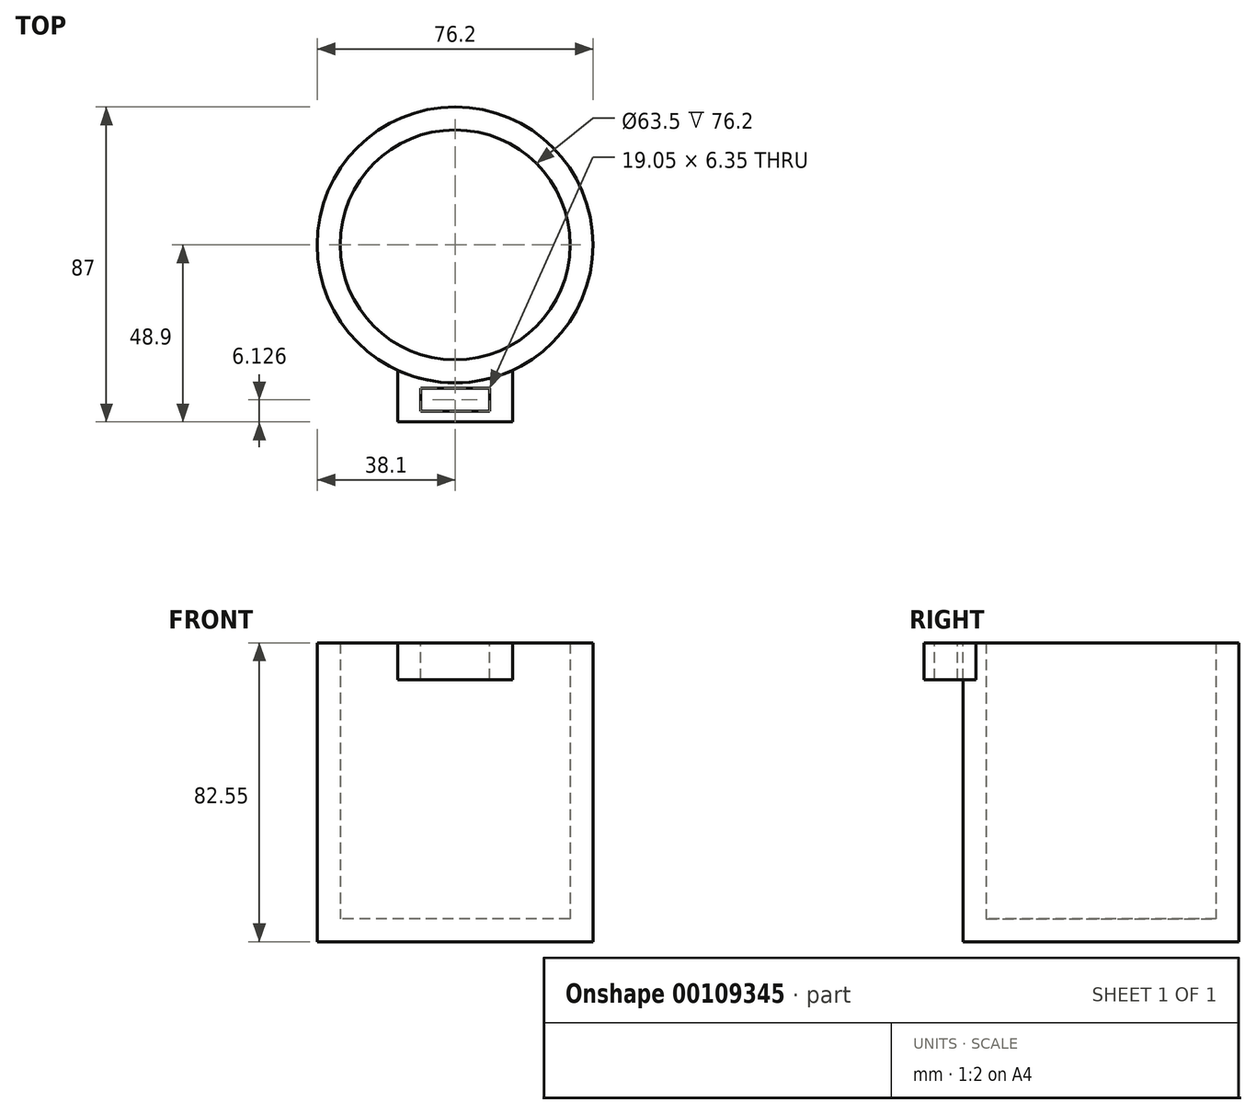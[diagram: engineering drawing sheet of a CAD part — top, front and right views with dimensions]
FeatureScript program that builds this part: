
annotation { "Feature Type Name" : "Feature", "Feature Type Description" : "" }
export const myFeature = defineFeature(function(context is Context, id is Id, definition is map)
    precondition{}
    {
        {
            var Q0;
            Q0=qCreatedBy(makeId("Top.planeOp"),FACE);
            var sketch = newSketch(context, id + "F0", { "sketchPlane" : qUnion([Q0])});
            skCircle(sketch, "E0", {"center": v(0, 0) * mm, "radius": 38.1 * mm});
            skSolve(sketch);
        }
        {
            var Q0;
            Q0 = qSketchRegion(id + "F0", true);
            extrude(context, id + "F1", {"entities" : qUnion([Q0]), "depth" : 6.35 * mm});
        }
        {
            var Q0;
            Q0=makeQuery(id+"F1.opExtrude","CAP_FACE",FACE,{"disambiguationData":[OSD([sQuery(id+"F0.wireOp",EDGE,"E0")])],"isStart":false});
            var sketch = newSketch(context, id + "F2", { "sketchPlane" : qUnion([Q0])});
            skCircle(sketch, "E1", {"center": v(0, 0) * mm, "radius": 38.1 * mm});
            skCircle(sketch, "E2", {"center": v(0, 0) * mm, "radius": 31.75 * mm});
            skSolve(sketch);
        }
        {
            var Q0;
            Q0 = qSketchRegion(id + "F2", true);
            extrude(context, id + "F3", {"entities" : qUnion([Q0]), "operationType" : NewBodyOperationType.ADD, "depth" : 76.2 * mm});
        }
        {
            var Q0;
            Q0=makeQuery(id+"F3.opExtrude","CAP_FACE",FACE,{"disambiguationData":[OSD([sQuery(id+"F2.wireOp",EDGE,"E1"),sQuery(id+"F2.wireOp",EDGE,"E2")])],"isStart":false});
            var sketch = newSketch(context, id + "F4", { "sketchPlane" : qUnion([Q0])});
            skLineSegment(sketch, "E3.top", {"start": v(15.88, -48.9) * mm, "end": v(-15.88, -48.9) * mm});
            skPoint(sketch, "E4.middle", {"position": v(0, -38.1) * mm});
            skLineSegment(sketch, "E5.bottom", {"start": v(9.53, -39.6) * mm, "end": v(-9.52, -39.6) * mm});
            skLineSegment(sketch, "E5.top", {"start": v(9.53, -45.95) * mm, "end": v(-9.52, -45.95) * mm});
            skLineSegment(sketch, "E5.left", {"start": v(9.53, -39.6) * mm, "end": v(9.53, -45.95) * mm});
            skLineSegment(sketch, "E5.right", {"start": v(-9.52, -39.6) * mm, "end": v(-9.52, -45.95) * mm});
            skPoint(sketch, "E5.middle", {"position": v(0, -42.77) * mm});
            skPoint(sketch, "E5.middle.positionSnap0", {"position": v(0, -48.9) * mm});
            skPoint(sketch, "E5.centerSnap0", {"position": v(0, -48.9) * mm});
            skLineSegment(sketch, "E6", {"start": v(-15.88, -48.9) * mm, "end": v(-15.88, -34.64) * mm});
            skLineSegment(sketch, "E7", {"start": v(15.88, -48.9) * mm, "end": v(15.88, -34.64) * mm});
            skArc(sketch, "E8", {"start": v(-15.88, -34.64) * mm, "mid": v(0, -38.1) * mm, "end": v(15.88, -34.64) * mm});
            skSolve(sketch);
        }
        {
            var Q0;
            Q0 = qSketchRegion(id + "F4", true);
            extrude(context, id + "F5", {"entities" : qUnion([Q0]), "oppositeDirection" : true, "depth" : 10.16 * mm});
        }
    });
